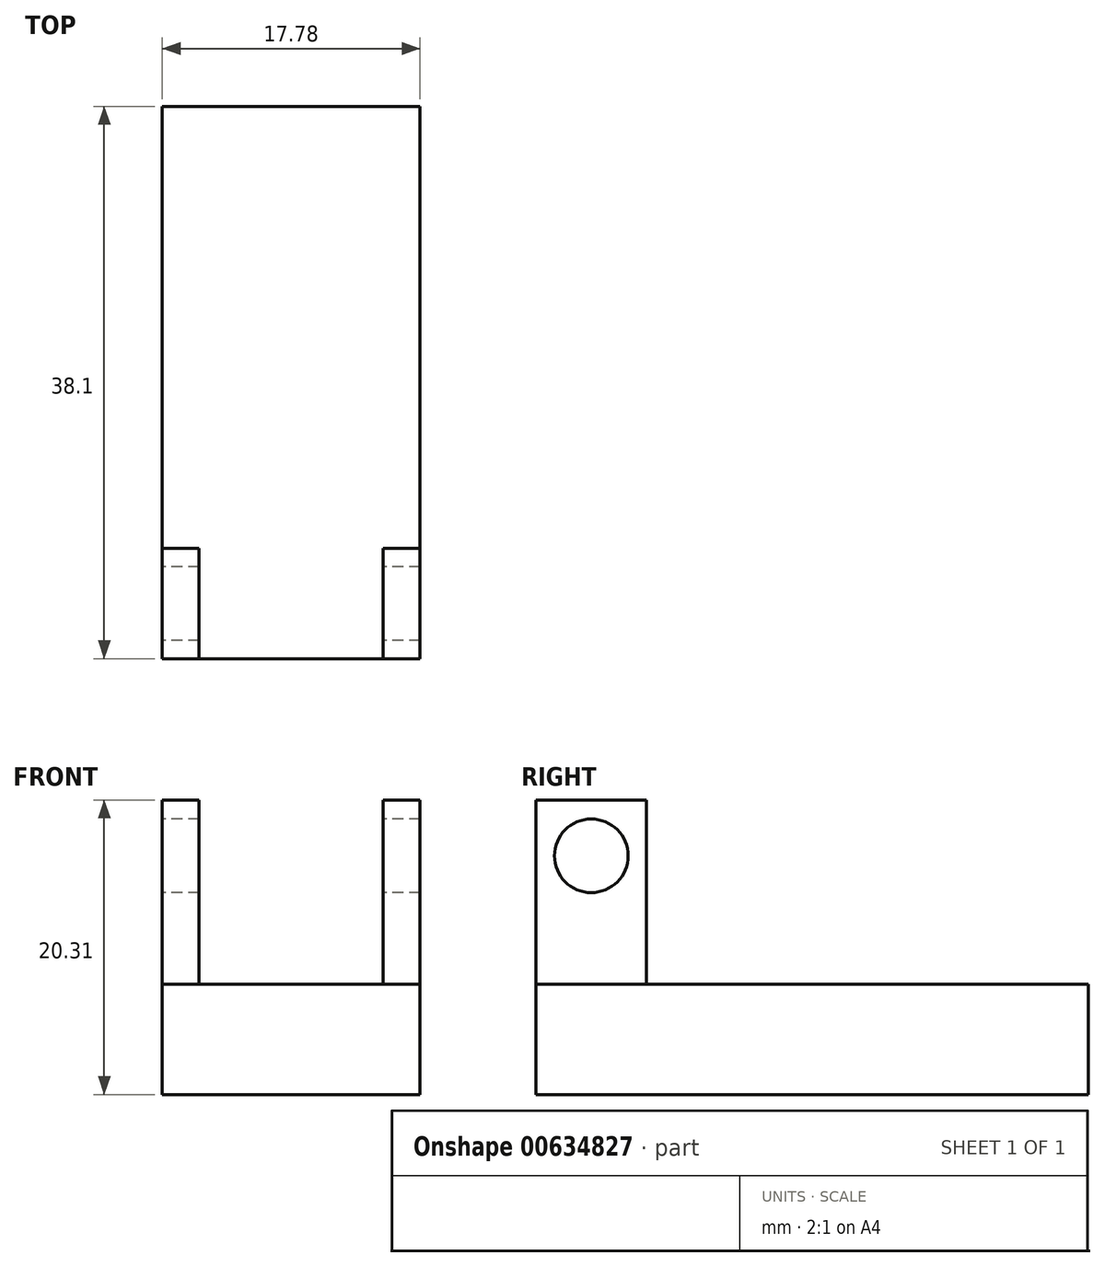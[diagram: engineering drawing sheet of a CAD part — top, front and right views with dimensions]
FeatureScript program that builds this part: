
annotation { "Feature Type Name" : "Feature", "Feature Type Description" : "" }
export const myFeature = defineFeature(function(context is Context, id is Id, definition is map)
    precondition{}
    {
        {
            var Q0;
            Q0=qCreatedBy(makeId("Top.planeOp"),FACE);
            var sketch = newSketch(context, id + "F0", { "sketchPlane" : qUnion([Q0])});
            skLineSegment(sketch, "E0.bottom", {"start": v(8.89, 0) * mm, "end": v(-8.9, 0) * mm});
            skLineSegment(sketch, "E0.top", {"start": v(8.9, 38.1) * mm, "end": v(-8.89, 38.1) * mm});
            skLineSegment(sketch, "E0.left", {"start": v(8.89, 0) * mm, "end": v(8.9, 38.1) * mm});
            skLineSegment(sketch, "E0.right", {"start": v(-8.9, 0) * mm, "end": v(-8.89, 38.1) * mm});
            skPoint(sketch, "E0.middle", {"position": v(0, 19.05) * mm});
            skSolve(sketch);
        }
        {
            var Q0;
            Q0=makeQuery(id+"F0.imprint","IMPRINT",FACE,{"disambiguationData":[TD([[makeQuery(id+"F0.imprint","IMPRINT",EDGE,{"derivedFrom":sQuery(id+"F0.wireOp",EDGE,"E0.bottom")}),-1.0]])]});
            extrude(context, id + "F1", {"entities" : qUnion([Q0]), "endBound" : BoundingType.SYMMETRIC, "depth" : 7.62 * mm, "offsetDistance" : 25.4 * mm});
        }
        {
            var Q0;
            Q0=qCreatedBy(makeId("Right.planeOp"),FACE);
            var sketch = newSketch(context, id + "F2", { "sketchPlane" : qUnion([Q0])});
            skLineSegment(sketch, "E1.bottom", {"start": v(0, 4.12) * mm, "end": v(7.62, 4.12) * mm});
            skLineSegment(sketch, "E1.top", {"start": v(0, 16.82) * mm, "end": v(7.62, 16.82) * mm});
            skLineSegment(sketch, "E1.left", {"start": v(0, 4.12) * mm, "end": v(0, 16.82) * mm});
            skLineSegment(sketch, "E1.right", {"start": v(7.62, 4.12) * mm, "end": v(7.62, 16.82) * mm});
            skCircle(sketch, "E2", {"center": v(3.8, 12.97) * mm, "radius": 2.54 * mm});
            skPoint(sketch, "E2.centerSnap0", {"position": v(3.8, 16.82) * mm});
            skSolve(sketch);
        }
        {
            var Q0;
            Q0=makeQuery(id+"F2.imprint","IMPRINT",FACE,{"disambiguationData":[TD([[makeQuery(id+"F2.imprint","IMPRINT",EDGE,{"derivedFrom":sQuery(id+"F2.wireOp",EDGE,"E1.bottom")}),1.0]])]});
            extrude(context, id + "F3", {"entities" : qUnion([Q0]), "depth" : 2.54 * mm, "offsetDistance" : 25.4 * mm});
        }
        {
            var Q0;
            Q0=makeQuery(id+"F3.opExtrude","SWEPT_BODY",BODY,{"disambiguationData":[OSD([sQuery(id+"F2.wireOp",EDGE,"E1.bottom"),sQuery(id+"F2.wireOp",EDGE,"E1.top"),sQuery(id+"F2.wireOp",EDGE,"E1.left"),sQuery(id+"F2.wireOp",EDGE,"E1.right"),sQuery(id+"F2.wireOp",EDGE,"E2")])]});
            transform(context, id + "F4", {"entities" : qUnion([Q0]), "transformType" : TransformType.TRANSLATION_3D, "dx" : 6.35 * mm, "dy" : 0 * mm, "dz" : -0.32 * mm, "makeCopy" : true});
        }
        {
            var Q0;
            Q0=makeQuery(id+"F3.opExtrude","SWEPT_BODY",BODY,{"disambiguationData":[OSD([sQuery(id+"F2.wireOp",EDGE,"E1.bottom"),sQuery(id+"F2.wireOp",EDGE,"E1.top"),sQuery(id+"F2.wireOp",EDGE,"E1.left"),sQuery(id+"F2.wireOp",EDGE,"E1.right"),sQuery(id+"F2.wireOp",EDGE,"E2")])]});
            deleteBodies(context, id + "F5", {"entities" : qUnion([Q0])});
        }
        {
            var Q0;
            Q0=makeQuery(id+"F4.opPattern","COPY",BODY,{"derivedFrom":makeQuery(id+"F3.opExtrude","SWEPT_BODY",BODY,{"disambiguationData":[OSD([sQuery(id+"F2.wireOp",EDGE,"E1.bottom"),sQuery(id+"F2.wireOp",EDGE,"E1.top"),sQuery(id+"F2.wireOp",EDGE,"E1.left"),sQuery(id+"F2.wireOp",EDGE,"E1.right"),sQuery(id+"F2.wireOp",EDGE,"E2")])]}),"instanceName":"1"});
            transform(context, id + "F6", {"entities" : qUnion([Q0]), "transformType" : TransformType.TRANSLATION_3D, "dx" : -15.24 * mm, "dy" : 0 * mm, "dz" : 0 * mm, "makeCopy" : true});
        }
    });
